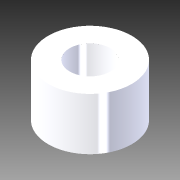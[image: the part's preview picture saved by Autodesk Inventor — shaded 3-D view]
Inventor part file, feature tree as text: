
AUTODESK INVENTOR PART (.ipt)
format: ipt  version: 2012 (Build 160160000, 160)  size: 89,088 bytes
history: native  units: in
note: dims shown in document units (in); Inventor stores cm internally (conversion verified against a paired STEP export)
features: other x1, imported_body x1, extrude x1, sketch x1
ambient origin geometry x8: Origin, YZ Plane, XZ Plane, XY Plane, X Axis, Y Axis, Z Axis, Center Point
feature tree (4):
  parser-record x1  (decoder bookkeeping rows leaked as tree rows — omitted from the tree; the rows remain in map.json)
  imported_body  "Base1"
  extrude  "Extrusion1"  Depth=0.5in
  sketch  "Sketch1"  dims[d0=0.4in d1=0.5in d2=1.0in d3=0.0in]
